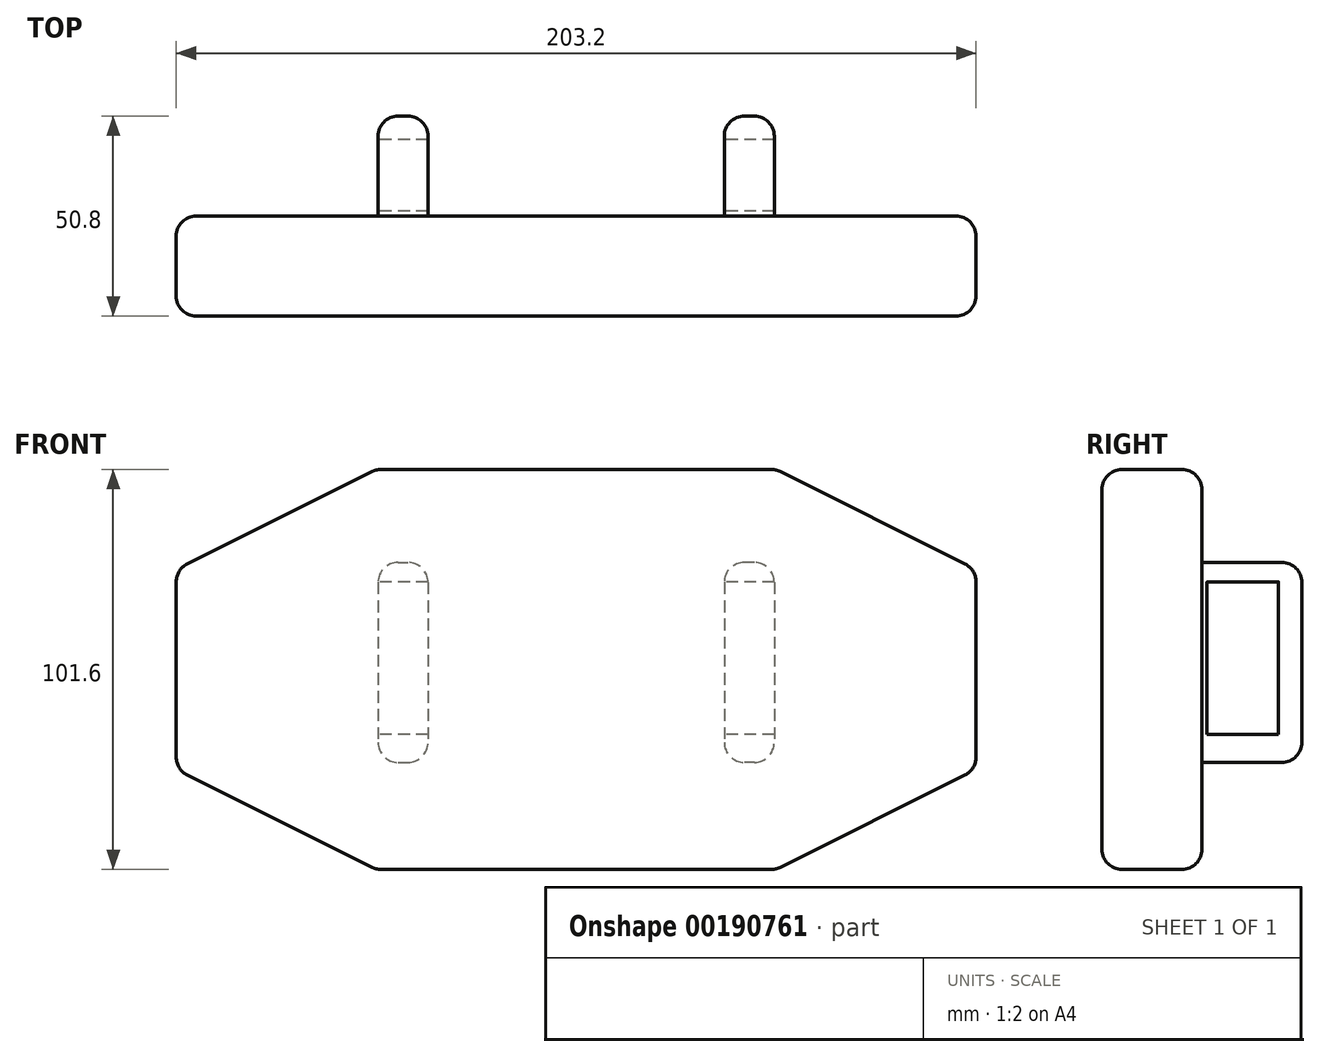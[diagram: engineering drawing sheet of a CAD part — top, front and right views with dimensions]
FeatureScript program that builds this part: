
annotation { "Feature Type Name" : "Feature", "Feature Type Description" : "" }
export const myFeature = defineFeature(function(context is Context, id is Id, definition is map)
    precondition{}
    {
        {
            var Q0;
            Q0=qCreatedBy(makeId("Front.planeOp"),FACE);
            var sketch = newSketch(context, id + "F0", { "sketchPlane" : qUnion([Q0])});
            skLineSegment(sketch, "E0.bottom", {"start": v(-50.8, -50.8) * mm, "end": v(50.8, -50.8) * mm});
            skLineSegment(sketch, "E0.top", {"start": v(-50.8, 50.8) * mm, "end": v(50.8, 50.8) * mm});
            skLineSegment(sketch, "E0.left", {"start": v(-101.6, -25.4) * mm, "end": v(-101.6, 25.4) * mm});
            skLineSegment(sketch, "E0.right", {"start": v(101.6, -25.4) * mm, "end": v(101.6, 25.4) * mm});
            skPoint(sketch, "E0.middle", {"position": v(0, 0) * mm});
            skPoint(sketch, "E1", {"position": v(-101.6, 25.4) * mm});
            skLineSegment(sketch, "E2", {"start": v(-139.4, 0) * mm, "end": v(166.24, 0) * mm, "construction": true});
            skLineSegment(sketch, "E3", {"start": v(0, 86) * mm, "end": v(0, -83.95) * mm, "construction": true});
            skPoint(sketch, "E3.endSnap0", {"position": v(0, -50.8) * mm});
            skPoint(sketch, "E4.MirrorP", {"position": v(101.6, 25.4) * mm});
            skPoint(sketch, "E5.MirrorP", {"position": v(-101.6, -25.4) * mm});
            skPoint(sketch, "E6.MirrorP", {"position": v(101.6, -25.4) * mm});
            skPoint(sketch, "E7", {"position": v(-50.8, 50.8) * mm});
            skPoint(sketch, "E8.MirrorP", {"position": v(50.8, 50.8) * mm});
            skPoint(sketch, "E9.MirrorP", {"position": v(-50.8, -50.8) * mm});
            skPoint(sketch, "E10.MirrorP", {"position": v(50.8, -50.8) * mm});
            skLineSegment(sketch, "E11", {"start": v(-101.6, 25.4) * mm, "end": v(-50.8, 50.8) * mm});
            skLineSegment(sketch, "E12", {"start": v(50.8, 50.8) * mm, "end": v(101.6, 25.4) * mm});
            skLineSegment(sketch, "E13", {"start": v(101.6, -25.4) * mm, "end": v(50.8, -50.8) * mm});
            skLineSegment(sketch, "E14", {"start": v(-50.8, -50.8) * mm, "end": v(-101.6, -25.4) * mm});
            skPoint(sketch, "E15.orphan", {"position": v(-101.6, 50.8) * mm});
            skPoint(sketch, "E16.orphan", {"position": v(101.6, 50.8) * mm});
            skPoint(sketch, "E17.orphan", {"position": v(101.6, -50.8) * mm});
            skPoint(sketch, "E18.orphan", {"position": v(-101.6, -50.8) * mm});
            skSolve(sketch);
        }
        {
            var Q0;
            Q0 = qSketchRegion(id + "F0", true);
            extrude(context, id + "F1", {"entities" : qUnion([Q0]), "depth" : 25.4 * mm});
        }
        {
            var Q0;
            Q0=makeQuery(id+"F1.opExtrude","CAP_EDGE",EDGE,{"disambiguationData":[OSD([sQuery(id+"F0.wireOp",EDGE,"E11")])],"isStart":false});
            var Q1;
            Q1=makeQuery(id+"F1.opExtrude","CAP_EDGE",EDGE,{"disambiguationData":[OSD([sQuery(id+"F0.wireOp",EDGE,"E0.top")])],"isStart":false});
            var Q2;
            Q2=makeQuery(id+"F1.opExtrude","CAP_EDGE",EDGE,{"disambiguationData":[OSD([sQuery(id+"F0.wireOp",EDGE,"E12")])],"isStart":false});
            var Q3;
            Q3=makeQuery(id+"F1.opExtrude","CAP_EDGE",EDGE,{"disambiguationData":[OSD([sQuery(id+"F0.wireOp",EDGE,"E0.right")])],"isStart":false});
            var Q4;
            Q4=makeQuery(id+"F1.opExtrude","CAP_FACE",FACE,{"disambiguationData":[OSD([sQuery(id+"F0.wireOp",EDGE,"E0.bottom"),sQuery(id+"F0.wireOp",EDGE,"E0.top"),sQuery(id+"F0.wireOp",EDGE,"E0.left"),sQuery(id+"F0.wireOp",EDGE,"E0.right"),sQuery(id+"F0.wireOp",EDGE,"E11"),sQuery(id+"F0.wireOp",EDGE,"E12"),sQuery(id+"F0.wireOp",EDGE,"E13"),sQuery(id+"F0.wireOp",EDGE,"E14")])],"isStart":false});
            var Q5;
            Q5=makeQuery(id+"F1.opExtrude","SWEPT_EDGE",EDGE,{"disambiguationData":[OSD([sQuery(id+"F0.wireOp",EDGE,"E0.bottom"),sQuery(id+"F0.wireOp",EDGE,"E14")])]});
            var Q6;
            Q6=makeQuery(id+"F1.opExtrude","SWEPT_EDGE",EDGE,{"disambiguationData":[OSD([sQuery(id+"F0.wireOp",EDGE,"E0.left"),sQuery(id+"F0.wireOp",EDGE,"E14")])]});
            var Q7;
            Q7=makeQuery(id+"F1.opExtrude","SWEPT_EDGE",EDGE,{"disambiguationData":[OSD([sQuery(id+"F0.wireOp",EDGE,"E0.left"),sQuery(id+"F0.wireOp",EDGE,"E11")])]});
            var Q8;
            Q8=makeQuery(id+"F1.opExtrude","SWEPT_EDGE",EDGE,{"disambiguationData":[OSD([sQuery(id+"F0.wireOp",EDGE,"E0.top"),sQuery(id+"F0.wireOp",EDGE,"E11")])]});
            var Q9;
            Q9=makeQuery(id+"F1.opExtrude","SWEPT_EDGE",EDGE,{"disambiguationData":[OSD([sQuery(id+"F0.wireOp",EDGE,"E0.top"),sQuery(id+"F0.wireOp",EDGE,"E12")])]});
            var Q10;
            Q10=makeQuery(id+"F1.opExtrude","SWEPT_EDGE",EDGE,{"disambiguationData":[OSD([sQuery(id+"F0.wireOp",EDGE,"E0.right"),sQuery(id+"F0.wireOp",EDGE,"E12")])]});
            var Q11;
            Q11=makeQuery(id+"F1.opExtrude","SWEPT_EDGE",EDGE,{"disambiguationData":[OSD([sQuery(id+"F0.wireOp",EDGE,"E0.right"),sQuery(id+"F0.wireOp",EDGE,"E13")])]});
            var Q12;
            Q12=makeQuery(id+"F1.opExtrude","SWEPT_EDGE",EDGE,{"disambiguationData":[OSD([sQuery(id+"F0.wireOp",EDGE,"E0.bottom"),sQuery(id+"F0.wireOp",EDGE,"E13")])]});
            fillet(context, id + "F2", {"entities" : qUnion([Q0, Q1, Q2, Q3, Q4, Q5, Q6, Q7, Q8, Q9, Q10, Q11, Q12]), "radius" : 5.08 * mm, "tangentPropagation" : true, "allowEdgeOverflow" : false});
        }
        {
            var Q0;
            Q0=makeQuery(id+"F1.opExtrude","CAP_FACE",FACE,{"disambiguationData":[OSD([sQuery(id+"F0.wireOp",EDGE,"E0.bottom"),sQuery(id+"F0.wireOp",EDGE,"E0.top"),sQuery(id+"F0.wireOp",EDGE,"E0.left"),sQuery(id+"F0.wireOp",EDGE,"E0.right"),sQuery(id+"F0.wireOp",EDGE,"E11"),sQuery(id+"F0.wireOp",EDGE,"E12"),sQuery(id+"F0.wireOp",EDGE,"E13"),sQuery(id+"F0.wireOp",EDGE,"E14")])],"isStart":true});
            fillet(context, id + "F3", {"entities" : qUnion([Q0]), "radius" : 5.08 * mm, "tangentPropagation" : true, "allowEdgeOverflow" : false});
        }
        {
            var Q0;
            Q0=makeQuery(id+"F1.opExtrude","CAP_FACE",FACE,{"disambiguationData":[OSD([sQuery(id+"F0.wireOp",EDGE,"E0.bottom"),sQuery(id+"F0.wireOp",EDGE,"E0.top"),sQuery(id+"F0.wireOp",EDGE,"E0.left"),sQuery(id+"F0.wireOp",EDGE,"E0.right"),sQuery(id+"F0.wireOp",EDGE,"E11"),sQuery(id+"F0.wireOp",EDGE,"E12"),sQuery(id+"F0.wireOp",EDGE,"E13"),sQuery(id+"F0.wireOp",EDGE,"E14")])],"isStart":true});
            var sketch = newSketch(context, id + "F4", { "sketchPlane" : qUnion([Q0])});
            skLineSegment(sketch, "E19.bottom", {"start": v(-50.34, 27.2) * mm, "end": v(-37.64, 27.2) * mm});
            skLineSegment(sketch, "E19.top", {"start": v(-50.34, -23.6) * mm, "end": v(-37.64, -23.6) * mm});
            skLineSegment(sketch, "E19.left", {"start": v(-50.34, 27.2) * mm, "end": v(-50.34, -23.6) * mm});
            skLineSegment(sketch, "E19.right", {"start": v(-37.64, 27.2) * mm, "end": v(-37.64, -23.6) * mm});
            skLineSegment(sketch, "E20", {"start": v(0, 65.3) * mm, "end": v(0, -61.62) * mm, "construction": true});
            skLineSegment(sketch, "E21.MirrorCS", {"start": v(37.64, 27.2) * mm, "end": v(37.64, -23.6) * mm});
            skLineSegment(sketch, "E22.MirrorCS", {"start": v(50.34, 27.2) * mm, "end": v(50.34, -23.6) * mm});
            skLineSegment(sketch, "E23.MirrorCS", {"start": v(50.34, 27.2) * mm, "end": v(37.64, 27.2) * mm});
            skLineSegment(sketch, "E24.MirrorCS", {"start": v(50.34, -23.6) * mm, "end": v(37.64, -23.6) * mm});
            skSolve(sketch);
        }
        {
            var Q0;
            Q0 = qSketchRegion(id + "F4", true);
            extrude(context, id + "F5", {"entities" : qUnion([Q0]), "operationType" : NewBodyOperationType.ADD, "depth" : 25.4 * mm});
        }
        {
            var Q0;
            Q0=makeQuery(id+"F5.opExtrude","SWEPT_FACE",FACE,{"disambiguationData":[OSD([sQuery(id+"F4.wireOp",EDGE,"E22.MirrorCS")])]});
            var sketch = newSketch(context, id + "F6", { "sketchPlane" : qUnion([Q0])});
            skLineSegment(sketch, "E25.bottom", {"start": v(-1.3, 22.28) * mm, "end": v(-19.42, 22.28) * mm});
            skLineSegment(sketch, "E25.top", {"start": v(-1.3, -16.54) * mm, "end": v(-19.42, -16.54) * mm});
            skLineSegment(sketch, "E25.left", {"start": v(-1.3, 22.28) * mm, "end": v(-1.3, -16.54) * mm});
            skLineSegment(sketch, "E25.right", {"start": v(-19.42, 22.28) * mm, "end": v(-19.42, -16.54) * mm});
            skSolve(sketch);
        }
        {
            var Q0;
            Q0 = qSketchRegion(id + "F6", true);
            extrude(context, id + "F7", {"entities" : qUnion([Q0]), "operationType" : NewBodyOperationType.REMOVE, "oppositeDirection" : true, "depth" : 254 * mm});
        }
        {
            var Q0;
            Q0=makeQuery(id+"F5.opExtrude","CAP_FACE",FACE,{"disambiguationData":[OSD([sQuery(id+"F4.wireOp",EDGE,"E19.bottom"),sQuery(id+"F4.wireOp",EDGE,"E19.top"),sQuery(id+"F4.wireOp",EDGE,"E19.left"),sQuery(id+"F4.wireOp",EDGE,"E19.right")])],"isStart":false});
            var Q1;
            Q1=makeQuery(id+"F5.opExtrude","SWEPT_EDGE",EDGE,{"disambiguationData":[OSD([sQuery(id+"F4.wireOp",EDGE,"E19.top"),sQuery(id+"F4.wireOp",EDGE,"E19.left")])]});
            var Q2;
            Q2=makeQuery(id+"F5.opExtrude","SWEPT_EDGE",EDGE,{"disambiguationData":[OSD([sQuery(id+"F4.wireOp",EDGE,"E19.top"),sQuery(id+"F4.wireOp",EDGE,"E19.right")])]});
            var Q3;
            Q3=makeQuery(id+"F5.opExtrude","SWEPT_EDGE",EDGE,{"disambiguationData":[OSD([sQuery(id+"F4.wireOp",EDGE,"E19.bottom"),sQuery(id+"F4.wireOp",EDGE,"E19.right")])]});
            var Q4;
            Q4=makeQuery(id+"F5.opExtrude","SWEPT_EDGE",EDGE,{"disambiguationData":[OSD([sQuery(id+"F4.wireOp",EDGE,"E19.bottom"),sQuery(id+"F4.wireOp",EDGE,"E19.left")])]});
            fillet(context, id + "F8", {"entities" : qUnion([Q0, Q1, Q2, Q3, Q4]), "radius" : 5.08 * mm, "tangentPropagation" : true, "allowEdgeOverflow" : false});
        }
        {
            var Q0;
            Q0=makeQuery(id+"F5.opExtrude","CAP_FACE",FACE,{"disambiguationData":[OSD([sQuery(id+"F4.wireOp",EDGE,"E21.MirrorCS"),sQuery(id+"F4.wireOp",EDGE,"E22.MirrorCS"),sQuery(id+"F4.wireOp",EDGE,"E23.MirrorCS"),sQuery(id+"F4.wireOp",EDGE,"E24.MirrorCS")])],"isStart":false});
            var Q1;
            Q1=makeQuery(id+"F5.opExtrude","SWEPT_EDGE",EDGE,{"disambiguationData":[OSD([sQuery(id+"F4.wireOp",EDGE,"E21.MirrorCS"),sQuery(id+"F4.wireOp",EDGE,"E24.MirrorCS")])]});
            var Q2;
            Q2=makeQuery(id+"F5.opExtrude","SWEPT_EDGE",EDGE,{"disambiguationData":[OSD([sQuery(id+"F4.wireOp",EDGE,"E22.MirrorCS"),sQuery(id+"F4.wireOp",EDGE,"E24.MirrorCS")])]});
            var Q3;
            Q3=makeQuery(id+"F5.opExtrude","SWEPT_EDGE",EDGE,{"disambiguationData":[OSD([sQuery(id+"F4.wireOp",EDGE,"E21.MirrorCS"),sQuery(id+"F4.wireOp",EDGE,"E23.MirrorCS")])]});
            var Q4;
            Q4=makeQuery(id+"F5.opExtrude","SWEPT_EDGE",EDGE,{"disambiguationData":[OSD([sQuery(id+"F4.wireOp",EDGE,"E22.MirrorCS"),sQuery(id+"F4.wireOp",EDGE,"E23.MirrorCS")])]});
            fillet(context, id + "F9", {"entities" : qUnion([Q0, Q1, Q2, Q3, Q4]), "radius" : 5.08 * mm, "tangentPropagation" : true, "allowEdgeOverflow" : false});
        }
    });
